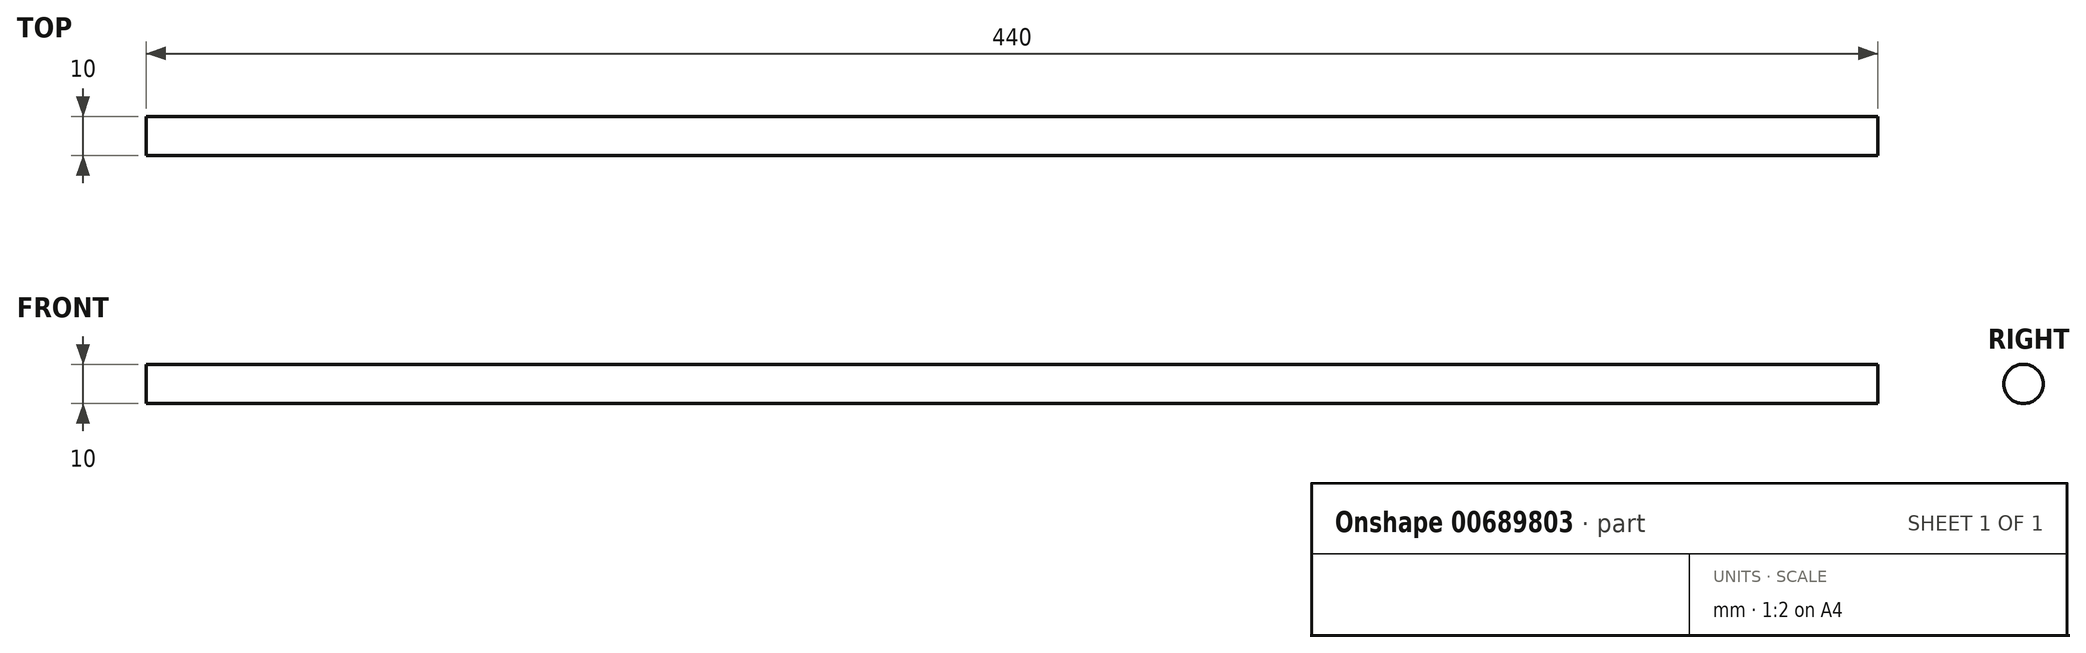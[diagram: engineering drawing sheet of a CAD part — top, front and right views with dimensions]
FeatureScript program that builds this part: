
annotation { "Feature Type Name" : "Feature", "Feature Type Description" : "" }
export const myFeature = defineFeature(function(context is Context, id is Id, definition is map)
    precondition{}
    {
        {
            var Q0;
            Q0=qCreatedBy(makeId("Right.planeOp"),FACE);
            var sketch = newSketch(context, id + "F0", { "sketchPlane" : qUnion([Q0])});
            skCircle(sketch, "E0", {"center": v(0, 0) * mm, "radius": 5 * mm});
            skSolve(sketch);
        }
        {
            var Q0;
            Q0=makeQuery(id+"F0.imprint","IMPRINT",FACE,{"disambiguationData":[TD([[makeQuery(id+"F0.imprint","IMPRINT",EDGE,{"derivedFrom":sQuery(id+"F0.wireOp",EDGE,"E0")}),1.0]])]});
            extrude(context, id + "F1", {"entities" : qUnion([Q0]), "depth" : 440 * mm, "offsetDistance" : 25 * mm});
        }
    });
